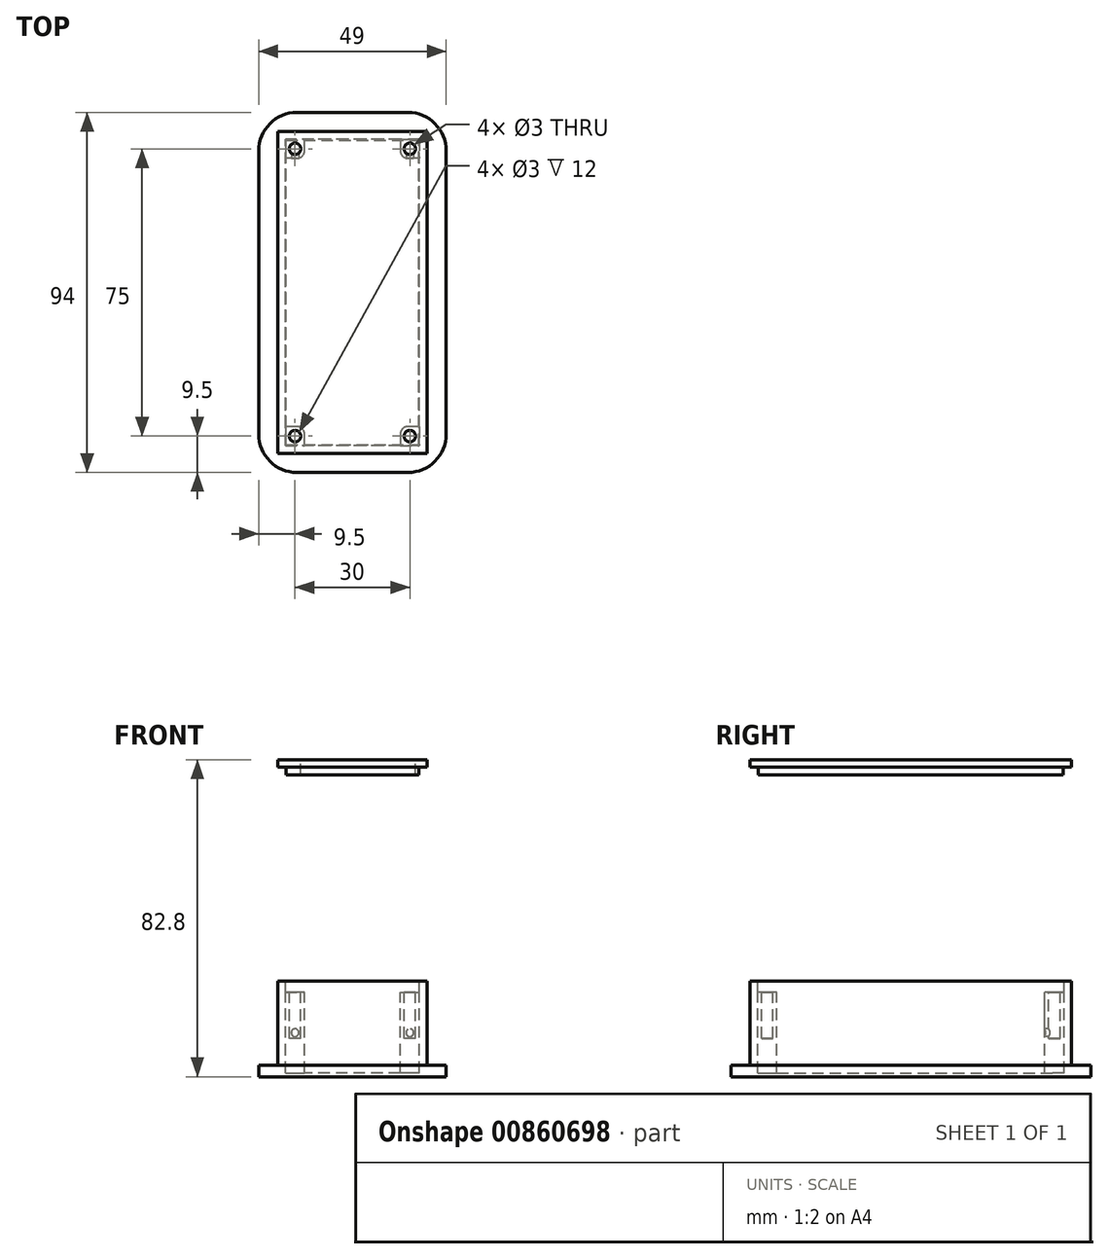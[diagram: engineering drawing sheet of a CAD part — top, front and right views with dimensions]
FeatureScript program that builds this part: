
annotation { "Feature Type Name" : "Feature", "Feature Type Description" : "" }
export const myFeature = defineFeature(function(context is Context, id is Id, definition is map)
    precondition{}
    {
        {
            var Q0;
            Q0=qCreatedBy(makeId("Top.planeOp"),FACE);
            var sketch = newSketch(context, id + "F0", { "sketchPlane" : qUnion([Q0])});
            skLineSegment(sketch, "E0.bottom", {"start": v(0, 0) * mm, "end": v(-39, 0) * mm});
            skLineSegment(sketch, "E0.top", {"start": v(0, 84) * mm, "end": v(-39, 84) * mm});
            skLineSegment(sketch, "E0.left", {"start": v(0, 0) * mm, "end": v(0, 84) * mm});
            skLineSegment(sketch, "E0.right", {"start": v(-39, 0) * mm, "end": v(-39, 84) * mm});
            skSolve(sketch);
        }
        {
            var Q0;
            Q0=makeQuery(id+"F0.imprint","IMPRINT",FACE,{"disambiguationData":[TD([[makeQuery(id+"F0.imprint","IMPRINT",EDGE,{"derivedFrom":sQuery(id+"F0.wireOp",EDGE,"E0.bottom")}),-1.0]])]});
            extrude(context, id + "F1", {"entities" : qUnion([Q0]), "depth" : 25 * mm, "offsetDistance" : 25 * mm});
        }
        {
            var Q0;
            Q0=makeQuery(id+"F1.opExtrude","CAP_FACE",FACE,{"disambiguationData":[OSD([sQuery(id+"F0.wireOp",EDGE,"E0.bottom"),sQuery(id+"F0.wireOp",EDGE,"E0.top"),sQuery(id+"F0.wireOp",EDGE,"E0.left"),sQuery(id+"F0.wireOp",EDGE,"E0.right")])],"isStart":false});
            var sketch = newSketch(context, id + "F2", { "sketchPlane" : qUnion([Q0])});
            skLineSegment(sketch, "E1.bottom", {"start": v(-7, 2) * mm, "end": v(-32, 2) * mm});
            skLineSegment(sketch, "E1.top", {"start": v(-7, 82) * mm, "end": v(-32, 82) * mm});
            skLineSegment(sketch, "E1.left", {"start": v(-2, 7) * mm, "end": v(-2, 77) * mm});
            skLineSegment(sketch, "E1.right", {"start": v(-37, 7) * mm, "end": v(-37, 77) * mm});
            skLineSegment(sketch, "E2.top", {"start": v(-37, 77) * mm, "end": v(-32, 77) * mm});
            skLineSegment(sketch, "E2.right", {"start": v(-32, 82) * mm, "end": v(-32, 77) * mm});
            skLineSegment(sketch, "E3.top", {"start": v(-2, 77) * mm, "end": v(-7, 77) * mm});
            skLineSegment(sketch, "E3.right", {"start": v(-7, 82) * mm, "end": v(-7, 77) * mm});
            skLineSegment(sketch, "E4.top", {"start": v(-37, 7) * mm, "end": v(-32, 7) * mm});
            skLineSegment(sketch, "E4.right", {"start": v(-32, 2) * mm, "end": v(-32, 7) * mm});
            skLineSegment(sketch, "E5.top", {"start": v(-2, 7) * mm, "end": v(-7, 7) * mm});
            skLineSegment(sketch, "E5.right", {"start": v(-7, 2) * mm, "end": v(-7, 7) * mm});
            skSolve(sketch);
        }
        {
            var Q0;
            Q0=makeQuery(id+"F2.imprint","IMPRINT",FACE,{"disambiguationData":[TD([[makeQuery(id+"F2.imprint","IMPRINT",EDGE,{"derivedFrom":sQuery(id+"F2.wireOp",EDGE,"E1.bottom")}),-1.0]])]});
            extrude(context, id + "F3", {"entities" : qUnion([Q0]), "operationType" : NewBodyOperationType.REMOVE, "oppositeDirection" : true, "depth" : 24 * mm, "offsetDistance" : 25 * mm});
        }
        {
            var Q0;
            Q0=qCreatedBy(makeId("Top.planeOp"),FACE);
            cPlane(context, id + "F4", {"entities" : qUnion([Q0]), "cplaneType" : CPlaneType.OFFSET, "offset" : 80.8 * mm, "width" : 150 * mm, "height" : 150 * mm});
        }
        {
            var Q0;
            Q0=makeQuery(id+"F1.opExtrude","CAP_FACE",FACE,{"disambiguationData":[OSD([sQuery(id+"F0.wireOp",EDGE,"E0.bottom"),sQuery(id+"F0.wireOp",EDGE,"E0.top"),sQuery(id+"F0.wireOp",EDGE,"E0.left"),sQuery(id+"F0.wireOp",EDGE,"E0.right")])],"isStart":false});
            var sketch = newSketch(context, id + "F5", { "sketchPlane" : qUnion([Q0])});
            skLineSegment(sketch, "E6.bottom", {"start": v(-37, 82) * mm, "end": v(-2, 82) * mm});
            skLineSegment(sketch, "E6.top", {"start": v(-37, 2) * mm, "end": v(-2, 2) * mm});
            skLineSegment(sketch, "E6.left", {"start": v(-37, 82) * mm, "end": v(-37, 2) * mm});
            skLineSegment(sketch, "E6.right", {"start": v(-2, 82) * mm, "end": v(-2, 2) * mm});
            skCircle(sketch, "E7", {"center": v(-34.5, 79.5) * mm, "radius": 1.5 * mm});
            skPoint(sketch, "E7.centerSnap0", {"position": v(-34.5, 77) * mm});
            skPoint(sketch, "E7.centerSnap1", {"position": v(-7, 79.5) * mm});
            skCircle(sketch, "E8", {"center": v(-4.5, 79.5) * mm, "radius": 1.5 * mm});
            skPoint(sketch, "E8.centerSnap0", {"position": v(-4.5, 77) * mm});
            skCircle(sketch, "E9", {"center": v(-4.5, 4.5) * mm, "radius": 1.5 * mm});
            skPoint(sketch, "E9.centerSnap0", {"position": v(-7, 4.5) * mm});
            skPoint(sketch, "E9.centerSnap1", {"position": v(-4.5, 7) * mm});
            skCircle(sketch, "E10", {"center": v(-34.5, 4.5) * mm, "radius": 1.5 * mm});
            skPoint(sketch, "E10.centerSnap0", {"position": v(-34.5, 7) * mm});
            skPoint(sketch, "E10.centerSnap1", {"position": v(-32, 4.5) * mm});
            skSolve(sketch);
        }
        {
            var Q0;
            Q0 = qSketchRegion(id + "F5", true);
            var Q1;
            Q1=makeQuery(id+"F5.imprint","IMPRINT",FACE,{"disambiguationData":[TD([[makeQuery(id+"F5.imprint","IMPRINT",EDGE,{"derivedFrom":sQuery(id+"F5.wireOp",EDGE,"E7")}),1.0]])]});
            var Q2;
            Q2=makeQuery(id+"F5.imprint","IMPRINT",FACE,{"disambiguationData":[TD([[makeQuery(id+"F5.imprint","IMPRINT",EDGE,{"derivedFrom":sQuery(id+"F5.wireOp",EDGE,"E8")}),1.0]])]});
            var Q3;
            Q3=makeQuery(id+"F5.imprint","IMPRINT",FACE,{"disambiguationData":[TD([[makeQuery(id+"F5.imprint","IMPRINT",EDGE,{"derivedFrom":sQuery(id+"F5.wireOp",EDGE,"E9")}),1.0]])]});
            var Q4;
            Q4=makeQuery(id+"F5.imprint","IMPRINT",FACE,{"disambiguationData":[TD([[makeQuery(id+"F5.imprint","IMPRINT",EDGE,{"derivedFrom":sQuery(id+"F5.wireOp",EDGE,"E10")}),1.0]])]});
            extrude(context, id + "F6", {"entities" : qUnion([Q0, Q1, Q2, Q3, Q4]), "operationType" : NewBodyOperationType.REMOVE, "oppositeDirection" : true, "depth" : 3 * mm, "offsetDistance" : 25 * mm});
        }
        {
            var Q0;
            Q0=makeQuery(id+"F5.imprint","IMPRINT",FACE,{"disambiguationData":[TD([[makeQuery(id+"F5.imprint","IMPRINT",EDGE,{"derivedFrom":sQuery(id+"F5.wireOp",EDGE,"E7")}),1.0]])]});
            var Q1;
            Q1=makeQuery(id+"F5.imprint","IMPRINT",FACE,{"disambiguationData":[TD([[makeQuery(id+"F5.imprint","IMPRINT",EDGE,{"derivedFrom":sQuery(id+"F5.wireOp",EDGE,"E8")}),1.0]])]});
            var Q2;
            Q2=makeQuery(id+"F5.imprint","IMPRINT",FACE,{"disambiguationData":[TD([[makeQuery(id+"F5.imprint","IMPRINT",EDGE,{"derivedFrom":sQuery(id+"F5.wireOp",EDGE,"E9")}),1.0]])]});
            var Q3;
            Q3=makeQuery(id+"F5.imprint","IMPRINT",FACE,{"disambiguationData":[TD([[makeQuery(id+"F5.imprint","IMPRINT",EDGE,{"derivedFrom":sQuery(id+"F5.wireOp",EDGE,"E10")}),1.0]])]});
            extrude(context, id + "F7", {"entities" : qUnion([Q0, Q1, Q2, Q3]), "operationType" : NewBodyOperationType.REMOVE, "oppositeDirection" : true, "depth" : 15 * mm, "offsetDistance" : 25 * mm});
        }
        {
            var Q0;
            Q0=makeQuery(id+"F3.boolean.opBoolean","COPY",EDGE,{"derivedFrom":makeQuery(id+"F3.opExtrude","SWEPT_EDGE",EDGE,{"disambiguationData":[OSD([sQuery(id+"F2.wireOp",EDGE,"E2.top"),sQuery(id+"F2.wireOp",EDGE,"E2.right")])]})});
            var Q1;
            Q1=makeQuery(id+"F3.boolean.opBoolean","COPY",EDGE,{"derivedFrom":makeQuery(id+"F3.opExtrude","SWEPT_EDGE",EDGE,{"disambiguationData":[OSD([sQuery(id+"F2.wireOp",EDGE,"E3.top"),sQuery(id+"F2.wireOp",EDGE,"E3.right")])]})});
            var Q2;
            Q2=makeQuery(id+"F3.boolean.opBoolean","COPY",EDGE,{"derivedFrom":makeQuery(id+"F3.opExtrude","SWEPT_EDGE",EDGE,{"disambiguationData":[OSD([sQuery(id+"F2.wireOp",EDGE,"E4.top"),sQuery(id+"F2.wireOp",EDGE,"E4.right")])]})});
            var Q3;
            Q3=makeQuery(id+"F3.boolean.opBoolean","COPY",EDGE,{"derivedFrom":makeQuery(id+"F3.opExtrude","SWEPT_EDGE",EDGE,{"disambiguationData":[OSD([sQuery(id+"F2.wireOp",EDGE,"E5.top"),sQuery(id+"F2.wireOp",EDGE,"E5.right")])]})});
            fillet(context, id + "F8", {"entities" : qUnion([Q0, Q1, Q2, Q3]), "radius" : 2 * mm, "tangentPropagation" : true, "allowEdgeOverflow" : false});
        }
        {
            var Q0;
            Q0=qCreatedBy(id+"F4.planeOp",FACE);
            var sketch = newSketch(context, id + "F9", { "sketchPlane" : qUnion([Q0])});
            skLineSegment(sketch, "E11.bottom", {"start": v(-39, 84) * mm, "end": v(0, 84) * mm});
            skLineSegment(sketch, "E11.top", {"start": v(-39, 0) * mm, "end": v(0, 0) * mm});
            skLineSegment(sketch, "E11.left", {"start": v(-39, 84) * mm, "end": v(-39, 0) * mm});
            skLineSegment(sketch, "E11.right", {"start": v(0, 84) * mm, "end": v(0, 0) * mm});
            skSolve(sketch);
        }
        {
            var Q0;
            Q0=makeQuery(id+"F9.imprint","IMPRINT",FACE,{"disambiguationData":[TD([[makeQuery(id+"F9.imprint","IMPRINT",EDGE,{"derivedFrom":sQuery(id+"F9.wireOp",EDGE,"E11.bottom")}),-1.0]])]});
            extrude(context, id + "F10", {"entities" : qUnion([Q0]), "depth" : 2 * mm, "offsetDistance" : 25 * mm});
        }
        {
            var Q0;
            Q0=makeQuery(id+"F10.opExtrude","CAP_FACE",FACE,{"disambiguationData":[OSD([sQuery(id+"F9.wireOp",EDGE,"E11.bottom"),sQuery(id+"F9.wireOp",EDGE,"E11.top"),sQuery(id+"F9.wireOp",EDGE,"E11.left"),sQuery(id+"F9.wireOp",EDGE,"E11.right")])],"isStart":true});
            var sketch = newSketch(context, id + "F11", { "sketchPlane" : qUnion([Q0])});
            skLineSegment(sketch, "E12.bottom", {"start": v(-37, -2) * mm, "end": v(-2, -2) * mm});
            skLineSegment(sketch, "E12.top", {"start": v(-37, -82) * mm, "end": v(-2, -82) * mm});
            skLineSegment(sketch, "E12.left", {"start": v(-37, -2) * mm, "end": v(-37, -82) * mm});
            skLineSegment(sketch, "E12.right", {"start": v(-2, -2) * mm, "end": v(-2, -82) * mm});
            skSolve(sketch);
        }
        {
            var Q0;
            Q0=makeQuery(id+"F11.imprint","IMPRINT",FACE,{"disambiguationData":[TD([[makeQuery(id+"F11.imprint","IMPRINT",EDGE,{"derivedFrom":sQuery(id+"F11.wireOp",EDGE,"E12.bottom")}),-1.0]])]});
            extrude(context, id + "F12", {"entities" : qUnion([Q0]), "operationType" : NewBodyOperationType.ADD, "depth" : 2 * mm, "offsetDistance" : 25 * mm});
        }
        {
            var Q0;
            Q0=makeQuery(id+"F1.opExtrude","CAP_FACE",FACE,{"disambiguationData":[OSD([sQuery(id+"F0.wireOp",EDGE,"E0.bottom"),sQuery(id+"F0.wireOp",EDGE,"E0.top"),sQuery(id+"F0.wireOp",EDGE,"E0.left"),sQuery(id+"F0.wireOp",EDGE,"E0.right")])],"isStart":true});
            var sketch = newSketch(context, id + "F13", { "sketchPlane" : qUnion([Q0])});
            skLineSegment(sketch, "E13.bottom", {"start": v(-44, 5) * mm, "end": v(5, 5) * mm});
            skLineSegment(sketch, "E13.top", {"start": v(-44, -89) * mm, "end": v(5, -89) * mm});
            skLineSegment(sketch, "E13.left", {"start": v(-44, 5) * mm, "end": v(-44, -89) * mm});
            skLineSegment(sketch, "E13.right", {"start": v(5, 5) * mm, "end": v(5, -89) * mm});
            skSolve(sketch);
        }
        {
            var Q0;
            Q0=makeQuery(id+"F13.imprint","IMPRINT",FACE,{"disambiguationData":[TD([[makeQuery(id+"F13.imprint","IMPRINT",EDGE,{"derivedFrom":sQuery(id+"F13.wireOp",EDGE,"E13.bottom")}),-1.0]])]});
            extrude(context, id + "F14", {"entities" : qUnion([Q0]), "operationType" : NewBodyOperationType.ADD, "oppositeDirection" : true, "depth" : 3 * mm, "offsetDistance" : 25 * mm});
        }
        {
            var Q0;
            Q0=makeQuery(id+"F14.opExtrude","SWEPT_EDGE",EDGE,{"disambiguationData":[OSD([sQuery(id+"F13.wireOp",EDGE,"E13.bottom"),sQuery(id+"F13.wireOp",EDGE,"E13.left")])]});
            var Q1;
            Q1=makeQuery(id+"F14.opExtrude","SWEPT_EDGE",EDGE,{"disambiguationData":[OSD([sQuery(id+"F13.wireOp",EDGE,"E13.bottom"),sQuery(id+"F13.wireOp",EDGE,"E13.right")])]});
            var Q2;
            Q2=makeQuery(id+"F14.opExtrude","SWEPT_EDGE",EDGE,{"disambiguationData":[OSD([sQuery(id+"F13.wireOp",EDGE,"E13.top"),sQuery(id+"F13.wireOp",EDGE,"E13.right")])]});
            var Q3;
            Q3=makeQuery(id+"F14.opExtrude","SWEPT_EDGE",EDGE,{"disambiguationData":[OSD([sQuery(id+"F13.wireOp",EDGE,"E13.top"),sQuery(id+"F13.wireOp",EDGE,"E13.left")])]});
            fillet(context, id + "F15", {"entities" : qUnion([Q0, Q1, Q2, Q3]), "radius" : 10 * mm, "tangentPropagation" : true, "allowEdgeOverflow" : false});
        }
        {
            var Q0;
            Q0=makeQuery(id+"F10.opExtrude","CAP_FACE",FACE,{"disambiguationData":[OSD([sQuery(id+"F9.wireOp",EDGE,"E11.bottom"),sQuery(id+"F9.wireOp",EDGE,"E11.top"),sQuery(id+"F9.wireOp",EDGE,"E11.left"),sQuery(id+"F9.wireOp",EDGE,"E11.right")])],"isStart":false});
            var sketch = newSketch(context, id + "F16", { "sketchPlane" : qUnion([Q0])});
            skCircle(sketch, "E14", {"center": v(-34.5, 79.5) * mm, "radius": 1.5 * mm});
            skCircle(sketch, "E15", {"center": v(-4.5, 79.5) * mm, "radius": 1.5 * mm});
            skCircle(sketch, "E16", {"center": v(-4.5, 4.5) * mm, "radius": 1.5 * mm});
            skCircle(sketch, "E17", {"center": v(-34.5, 4.5) * mm, "radius": 1.5 * mm});
            skSolve(sketch);
        }
        {
            var Q0;
            Q0 = qSketchRegion(id + "F16", true);
            extrude(context, id + "F17", {"entities" : qUnion([Q0]), "operationType" : NewBodyOperationType.REMOVE, "oppositeDirection" : true, "depth" : 25 * mm, "offsetDistance" : 25 * mm});
        }
        {
            var Q0;
            Q0=makeQuery(id+"F12.opExtrude","SWEPT_FACE",FACE,{"disambiguationData":[OSD([sQuery(id+"F11.wireOp",EDGE,"E12.right")])]});
            var Q1;
            Q1=makeQuery(id+"F12.opExtrude","SWEPT_FACE",FACE,{"disambiguationData":[OSD([sQuery(id+"F11.wireOp",EDGE,"E12.left")])]});
            extrude(context, id + "F18", {"entities" : qUnion([Q0, Q1]), "operationType" : NewBodyOperationType.REMOVE, "oppositeDirection" : true, "depth" : 0.2 * mm, "offsetDistance" : 25 * mm, "hasSecondDirection" : true, "secondDirectionOppositeDirection" : false, "secondDirectionDepth" : 0.2 * mm});
        }
        {
            var Q0;
            Q0=makeQuery(id+"F12.opExtrude","SWEPT_FACE",FACE,{"disambiguationData":[OSD([sQuery(id+"F11.wireOp",EDGE,"E12.top")])]});
            var Q1;
            Q1=makeQuery(id+"F12.opExtrude","SWEPT_FACE",FACE,{"disambiguationData":[OSD([sQuery(id+"F11.wireOp",EDGE,"E12.bottom")])]});
            extrude(context, id + "F19", {"entities" : qUnion([Q0, Q1]), "operationType" : NewBodyOperationType.REMOVE, "depth" : 0.2 * mm, "offsetDistance" : 25 * mm, "hasSecondDirection" : true, "secondDirectionOppositeDirection" : true, "secondDirectionDepth" : 0.2 * mm});
        }
        {
            var Q0;
            Q0=makeQuery(id+"F3.boolean.opBoolean","COPY",FACE,{"derivedFrom":makeQuery(id+"F3.opExtrude","SWEPT_FACE",FACE,{"disambiguationData":[OSD([sQuery(id+"F2.wireOp",EDGE,"E2.top")])]})});
            var sketch = newSketch(context, id + "F20", { "sketchPlane" : qUnion([Q0])});
            skLineSegment(sketch, "E18", {"start": v(-37, 11.5) * mm, "end": v(0.02, 11.5) * mm});
            skCircle(sketch, "E19", {"center": v(-34.5, 11.5) * mm, "radius": 1 * mm});
            skCircle(sketch, "E20", {"center": v(-4.5, 11.5) * mm, "radius": 1 * mm});
            skSolve(sketch);
        }
        {
            var Q0;
            {var subQ0=sQuery(id+"F20.wireOp",EDGE,"E19");var subQ1=sQuery(id+"F20.wireOp",EDGE,"E18");var subQ2=makeQuery(id+"F20.imprint","INTERSECT",VERTEX,{"disambiguationData":[OD(1.0)],"derivedFrom":[subQ1,subQ0]});Q0=makeQuery(id+"F20.imprint","IMPRINT",FACE,{"disambiguationData":[TD([[makeQuery(id+"F20.imprint","IMPRINT",EDGE,{"disambiguationData":[TD([[subQ2,-1.0]])],"derivedFrom":subQ1}),1.0]])]});}
            var Q1;
            {var subQ0=sQuery(id+"F20.wireOp",EDGE,"E19");var subQ1=sQuery(id+"F20.wireOp",EDGE,"E18");var subQ2=makeQuery(id+"F20.imprint","INTERSECT",VERTEX,{"disambiguationData":[OD(0.0)],"derivedFrom":[subQ1,subQ0]});Q1=makeQuery(id+"F20.imprint","IMPRINT",FACE,{"disambiguationData":[TD([[makeQuery(id+"F20.imprint","IMPRINT",EDGE,{"disambiguationData":[TD([[subQ2,1.0]])],"derivedFrom":subQ1}),1.0]])]});}
            var Q2;
            {var subQ0=sQuery(id+"F20.wireOp",EDGE,"E19");var subQ1=sQuery(id+"F20.wireOp",EDGE,"E18");var subQ2=makeQuery(id+"F20.imprint","INTERSECT",VERTEX,{"disambiguationData":[OD(1.0)],"derivedFrom":[subQ1,subQ0]});Q2=makeQuery(id+"F20.imprint","IMPRINT",FACE,{"disambiguationData":[TD([[makeQuery(id+"F20.imprint","IMPRINT",EDGE,{"disambiguationData":[TD([[subQ2,-1.0]])],"derivedFrom":subQ1}),-1.0]])]});}
            var Q3;
            {var subQ0=sQuery(id+"F20.wireOp",EDGE,"E19");var subQ1=sQuery(id+"F20.wireOp",EDGE,"E18");var subQ2=makeQuery(id+"F20.imprint","INTERSECT",VERTEX,{"disambiguationData":[OD(0.0)],"derivedFrom":[subQ1,subQ0]});Q3=makeQuery(id+"F20.imprint","IMPRINT",FACE,{"disambiguationData":[TD([[makeQuery(id+"F20.imprint","IMPRINT",EDGE,{"disambiguationData":[TD([[subQ2,1.0]])],"derivedFrom":subQ1}),-1.0]])]});}
            var Q4;
            {var subQ0=sQuery(id+"F20.wireOp",EDGE,"E20");var subQ1=sQuery(id+"F20.wireOp",EDGE,"E18");var subQ2=makeQuery(id+"F20.imprint","INTERSECT",VERTEX,{"disambiguationData":[OD(0.0)],"derivedFrom":[subQ1,subQ0]});Q4=makeQuery(id+"F20.imprint","IMPRINT",FACE,{"disambiguationData":[TD([[makeQuery(id+"F20.imprint","IMPRINT",EDGE,{"disambiguationData":[TD([[subQ2,-1.0]])],"derivedFrom":subQ1}),1.0]])]});}
            var Q5;
            {var subQ0=sQuery(id+"F20.wireOp",EDGE,"E20");var subQ1=sQuery(id+"F20.wireOp",EDGE,"E18");var subQ2=makeQuery(id+"F20.imprint","INTERSECT",VERTEX,{"disambiguationData":[OD(0.0)],"derivedFrom":[subQ1,subQ0]});Q5=makeQuery(id+"F20.imprint","IMPRINT",FACE,{"disambiguationData":[TD([[makeQuery(id+"F20.imprint","IMPRINT",EDGE,{"disambiguationData":[TD([[subQ2,-1.0]])],"derivedFrom":subQ1}),-1.0]])]});}
            extrude(context, id + "F21", {"entities" : qUnion([Q0, Q1, Q2, Q3, Q4, Q5]), "operationType" : NewBodyOperationType.REMOVE, "oppositeDirection" : true, "depth" : 2 * mm, "offsetDistance" : 25 * mm});
        }
    });
